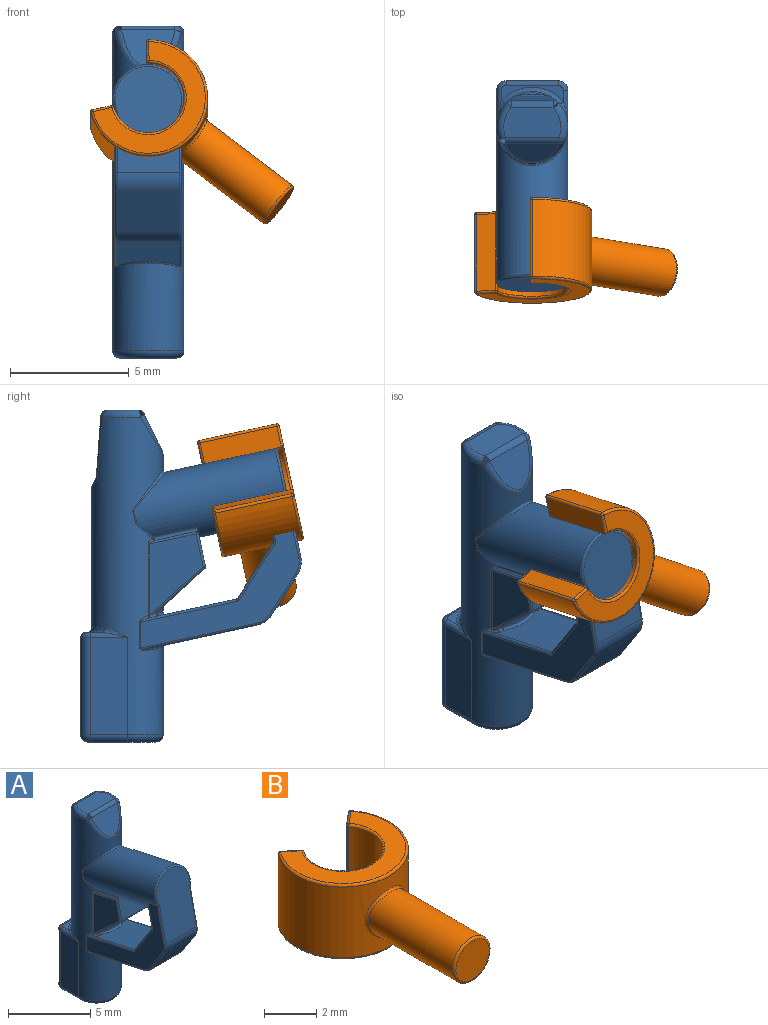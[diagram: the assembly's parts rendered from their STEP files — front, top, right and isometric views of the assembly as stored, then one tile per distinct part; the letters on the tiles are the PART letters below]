
ASSEMBLY  parts=2 mates=1
PART A: 146 faces, bbox 3.3x9.5x14 mm
  f0: bspline ~0.18x0.13mm, area 0mm2, adj f1,f4,f23,f53
  f1: cylinder r=0.1mm len=0.17mm, axis (1,0,0), area 0mm2, adj f0,f11,f53,f72
  f2: cylinder r=0.1mm len=0.18mm, axis (1,0,0), area 0mm2, adj f3,f11,f53,f69
  f3: bspline ~0.18x0.13mm, area 0mm2, adj f2,f18,f53,f71
  f4: bspline ~0.43x0.32mm, area 0.1mm2, adj f0,f23,f53,f77
  f5: plane 2.6x0.67mm, normal (0,0,1), area 0.6mm2, adj f60,f61,f62,f64,f66,f68
  f6: cylinder r=1.5mm len=1.72mm, axis (0,0,-1), area 0mm2, adj f22,f70
  f7: cylinder r=1.5mm len=13.36mm, axis (0,0,-1), area 80.6mm2, adj f15,f17,f20,f25,f27,f29,f32,f35
  f8: plane 3.42x2.25mm, normal (1,0,0), area 4.8mm2, adj f23,f26,f27,f28
  f9: plane 3.42x2.25mm, normal (-1,0,0), area 4.8mm2, adj f14,f16,f17,f18
  f10: plane 2.2x1.64mm, normal (0,-0.98,0.21), area 3mm2, adj f12,f16,f21,f26,f30,f33
  f11: plane 2.2x2.01mm, normal (0,-0.67,-0.74), area 5.5mm2, adj f1,f2,f18,f21,f22,f23
  f12: cylinder r=1.5mm len=6.87mm, axis (0,0.98,-0.21), area 45.5mm2, adj f10,f30,f32,f33,f35,f36,f37,f39
  f13: plane 4.52x2.83mm, normal (0,-0.98,0.21), area 11.5mm2, adj f36,f103,f104,f105,f106,f122,f123,f124
  f14: cylinder r=0.1mm len=2.07mm, axis (0,-0.98,0.21), area 0.3mm2, adj f9,f15,f16,f30
  f15: bspline ~0.29x0.26mm, area 0mm2, adj f7,f14,f17,f31
  f16: cylinder r=0.1mm len=1.5mm, axis (0,-0.21,-0.98), area 0.2mm2, adj f9,f10,f14,f19,f30
  f17: cylinder r=0.1mm len=3mm, axis (0,0,-1), area 0.2mm2, adj f7,f9,f15,f20
  f18: cylinder r=0.1mm len=2.33mm, axis (0,0.74,-0.67), area 0.4mm2, adj f3,f9,f11,f19,f20,f71
  f19: sphere r=0.1mm, area 0mm2, adj f16,f18,f21
  f20: bspline ~0.07x0.06mm, area 0mm2, adj f7,f17,f18,f73
  f21: cylinder r=0.1mm len=2.2mm, axis (-1,0,0), area 0.2mm2, adj f10,f11,f19,f24
  f22: bspline ~1.83x0.34mm, area 0.2mm2, adj f6,f11,f69,f72
  f23: cylinder r=0.1mm len=2.33mm, axis (0,-0.74,0.67), area 0.4mm2, adj f0,f4,f8,f11,f24,f25
  f24: sphere r=0.1mm, area 0mm2, adj f21,f23,f26
  f25: bspline ~0.1x0.08mm, area 0mm2, adj f7,f23,f27,f77
  f26: cylinder r=0.1mm len=1.5mm, axis (0,0.21,0.98), area 0.2mm2, adj f8,f10,f24,f28,f33
  f27: cylinder r=0.1mm len=3mm, axis (0,0,-1), area 0.2mm2, adj f7,f8,f25,f29
  f28: cylinder r=0.1mm len=2.07mm, axis (0,0.98,-0.21), area 0.3mm2, adj f8,f26,f29,f33
  f29: bspline ~0.32x0.28mm, area 0mm2, adj f7,f27,f28,f34
  f30: cylinder r=0.1mm len=1.86mm, axis (0,-0.98,0.21), area 0.4mm2, adj f10,f12,f14,f16,f31
  f31: sphere r=0.1mm, area 0mm2, adj f15,f30,f32
  f32: bspline ~0.91x0.75mm, area 0.1mm2, adj f7,f12,f31,f43
  f33: cylinder r=0.1mm len=1.86mm, axis (0,0.98,-0.21), area 0.4mm2, adj f10,f12,f26,f28,f34
  f34: sphere r=0.1mm, area 0mm2, adj f29,f33,f35
  f35: bspline ~0.91x0.75mm, area 0.1mm2, adj f7,f12,f34,f38
  f36: torus R=1.4mm, axis (0,0.98,-0.21), area 0.8mm2, adj f12,f13,f83,f87,f100,f101
  f37: bspline ~3x1.86mm, area 0.6mm2, adj f7,f12,f40,f41
  f38: bspline ~0.05x0.03mm, area 0mm2, adj f7,f35,f39
  f39: bspline ~0.56x0.15mm, area 0mm2, adj f7,f12,f38,f40
  f40: bspline ~0.05x0.03mm, area 0mm2, adj f7,f37,f39
  f41: bspline ~0.05x0.03mm, area 0mm2, adj f7,f37,f42
  f42: bspline ~0.56x0.15mm, area 0mm2, adj f7,f12,f41,f43
  f43: bspline ~0.05x0.03mm, area 0mm2, adj f7,f32,f42
  f44: plane 2.24x1.56mm, normal (0,-0.9,0.44), area 2.8mm2, adj f136,f139
  f45: plane 2.4x1.26mm, normal (0,0,1), area 2.8mm2, adj f131,f134,f135,f136
  f46: plane 2.6x1.82mm, normal (0,1,0.07), area 3.9mm2, adj f126,f129,f130,f131
  f47: plane 0.87x0.11mm, normal (0,0.81,0.58), area 0.1mm2, adj f125,f126
  f48: plane 2.86x2.4mm, normal (0,0,-1), area 6.2mm2, adj f140,f141,f142,f143,f144,f145
  f49: plane 6.67x6.39mm, normal (-1,0,0), area 11mm2, adj f74,f78,f81,f84,f87,f88,f90,f91
  f50: plane 4.56x2.62mm, normal (0,-0.21,-0.98), area 10.9mm2, adj f102,f112,f115,f118
  f51: plane 6.67x6.39mm, normal (1,0,0), area 11mm2, adj f80,f86,f89,f93,f95,f97,f99,f101
  f52: plane 2.6x1.34mm, normal (0,0.98,-0.21), area 2.4mm2, adj f91,f92,f96,f97
  f53: plane 3.65x2.64mm, normal (0,0.21,0.98), area 8.3mm2, adj f0,f1,f2,f3,f4,f70,f71,f75
  f54: plane 2.6x2.31mm, normal (0,0.84,0.54), area 7.1mm2, adj f84,f85,f92,f93
  f55: plane 2.62x1.68mm, normal (0,-0.84,-0.54), area 5.2mm2, adj f102,f103,f108,f120
  f56: plane 4.1x1.56mm, normal (1,0,0), area 6.4mm2, adj f7,f60,f65,f140
  f57: plane 4.1x1.56mm, normal (-1,0,0), area 6.4mm2, adj f7,f64,f67,f143
  f58: plane 4.1x2.2mm, normal (0,1,0), area 9mm2, adj f62,f65,f67,f144
  f59: bspline ~1.2x0.43mm, area 0.1mm2, adj f7,f60,f61
  f60: cylinder r=0.2mm len=1.56mm, axis (0,-1,0), area 0.3mm2, adj f5,f56,f59,f66
  f61: torus R=1.7mm, axis (0,0,-1), area 0.9mm2, adj f5,f7,f59,f63
  f62: cylinder r=0.2mm len=2.2mm, axis (1,0,0), area 0.7mm2, adj f5,f58,f66,f68
  f63: bspline ~1.2x0.43mm, area 0.1mm2, adj f7,f61,f64
  f64: cylinder r=0.2mm len=1.56mm, axis (0,1,0), area 0.3mm2, adj f5,f57,f63,f68
  f65: cylinder r=0.4mm len=4.1mm, axis (0,0,1), area 2.6mm2, adj f56,f58,f66,f142
  f66: torus R=0.2mm, axis (0,0,-1), area 0.2mm2, adj f5,f60,f62,f65
  f67: cylinder r=0.4mm len=4.1mm, axis (0,0,1), area 2.6mm2, adj f57,f58,f68,f145
  f68: torus R=0.2mm, axis (0,0,-1), area 0.2mm2, adj f5,f62,f64,f67
  f69: sphere r=0.1mm, area 0mm2, adj f2,f22,f70
  f70: bspline ~1.83x0.39mm, area 0.3mm2, adj f6,f53,f69,f72
  f71: bspline ~0.43x0.32mm, area 0.1mm2, adj f3,f18,f53,f73
  f72: sphere r=0.1mm, area 0mm2, adj f1,f22,f70
  f73: sphere r=0.1mm, area 0mm2, adj f20,f71,f75
  f74: cylinder r=0.1mm len=1.1mm, axis (0,0,-1), area 0mm2, adj f7,f49,f76,f109
  f75: bspline ~0.1x0.08mm, area 0mm2, adj f7,f53,f73,f76
  f76: bspline ~0.46x0.29mm, area 0mm2, adj f7,f74,f75,f78
  f77: sphere r=0.1mm, area 0mm2, adj f4,f25,f79
  f78: cylinder r=0.1mm len=4.05mm, axis (0,-0.98,0.21), area 0.6mm2, adj f49,f53,f76,f81
  f79: bspline ~0.1x0.08mm, area 0mm2, adj f7,f53,f77,f82
  f80: cylinder r=0.1mm len=1.1mm, axis (0,0,-1), area 0mm2, adj f7,f51,f82,f116
  f81: torus R=0.2mm, axis (-1,0,0), area 0mm2, adj f49,f78,f84,f85
  f82: bspline ~0.46x0.3mm, area 0mm2, adj f7,f79,f80,f86
  f83: bspline ~0.46x0.08mm, area 0mm2, adj f36,f87,f104
  f84: cylinder r=0.1mm len=2.36mm, axis (0,-0.54,0.84), area 0.4mm2, adj f49,f54,f81,f88
  f85: cylinder r=0.1mm len=2.6mm, axis (1,0,0), area 0.2mm2, adj f53,f54,f81,f89
  f86: cylinder r=0.1mm len=4.05mm, axis (0,-0.98,0.21), area 0.6mm2, adj f51,f53,f82,f89
  f87: bspline ~0.15x0.1mm, area 0mm2, adj f36,f49,f83,f90,f105
  f88: torus R=0.2mm, axis (-1,0,0), area 0mm2, adj f49,f84,f91,f92
  f89: torus R=0.2mm, axis (1,0,0), area 0mm2, adj f51,f85,f86,f93
  f90: cylinder r=0.1mm len=0.79mm, axis (0,0.98,-0.21), area 0mm2, adj f12,f49,f87,f94
  f91: cylinder r=0.1mm len=1.73mm, axis (0,0.21,0.98), area 0.2mm2, adj f49,f52,f88,f94
  f92: cylinder r=0.1mm len=2.6mm, axis (1,0,0), area 0.2mm2, adj f52,f54,f88,f95
  f93: cylinder r=0.1mm len=2.36mm, axis (0,0.54,-0.84), area 0.4mm2, adj f51,f54,f89,f95
  f94: bspline ~0.44x0.2mm, area 0mm2, adj f12,f90,f91,f96
  f95: torus R=0.2mm, axis (1,0,0), area 0mm2, adj f51,f92,f93,f97
  f96: torus R=1.6mm, axis (0,-0.98,0.21), area 0.5mm2, adj f12,f52,f94,f98
  f97: cylinder r=0.1mm len=1.73mm, axis (0,-0.21,-0.98), area 0.2mm2, adj f51,f52,f95,f98
  f98: bspline ~0.49x0.24mm, area 0mm2, adj f12,f96,f97,f99
  f99: cylinder r=0.1mm len=0.79mm, axis (0,0.98,-0.21), area 0mm2, adj f12,f51,f98,f101
  f100: bspline ~0.55x0.12mm, area 0mm2, adj f36,f101,f123
  f101: bspline ~0.15x0.1mm, area 0mm2, adj f36,f51,f99,f100,f124
  f102: cylinder r=1mm len=2.62mm, axis (-1,0,0), area 2.1mm2, adj f50,f55,f110,f119
  f103: cylinder r=1mm len=2.62mm, axis (-1,0,0), area 2.1mm2, adj f13,f55,f107,f121
  f104: bspline ~0.47x0.1mm, area 0mm2, adj f13,f83,f105
  f105: bspline ~0.18x0.11mm, area 0mm2, adj f13,f87,f104,f106
  f106: cylinder r=0.09mm len=2.59mm, axis (0,0.21,0.98), area 0.4mm2, adj f13,f49,f105,f107
  f107: torus R=0.91mm, axis (-1,0,0), area 0.1mm2, adj f49,f103,f106,f108
  f108: cylinder r=0.09mm len=1.73mm, axis (0,-0.54,0.84), area 0.3mm2, adj f49,f55,f107,f110
  f109: bspline ~0.11x0.1mm, area 0mm2, adj f74,f111,f112
  f110: torus R=0.91mm, axis (-1,0,0), area 0.1mm2, adj f49,f102,f108,f112
  f111: bspline ~0.1x0.06mm, area 0mm2, adj f7,f109,f113
  f112: cylinder r=0.09mm len=4.89mm, axis (0,-0.98,0.21), area 0.7mm2, adj f49,f50,f109,f110,f113
  f113: bspline ~0.37x0.18mm, area 0mm2, adj f7,f111,f112,f115
  f114: bspline ~0.1x0.06mm, area 0mm2, adj f7,f116,f117
  f115: bspline ~2.62x0.72mm, area 0.4mm2, adj f7,f50,f113,f117
  f116: bspline ~0.11x0.11mm, area 0mm2, adj f80,f114,f118
  f117: bspline ~0.38x0.18mm, area 0mm2, adj f7,f114,f115,f118
  f118: cylinder r=0.09mm len=4.89mm, axis (0,-0.98,0.21), area 0.7mm2, adj f50,f51,f116,f117,f119
  f119: torus R=0.91mm, axis (1,0,0), area 0.1mm2, adj f51,f102,f118,f120
  f120: cylinder r=0.09mm len=1.73mm, axis (0,0.54,-0.84), area 0.3mm2, adj f51,f55,f119,f121
  f121: torus R=0.91mm, axis (1,0,0), area 0.1mm2, adj f51,f103,f120,f122
  f122: cylinder r=0.09mm len=2.59mm, axis (0,-0.21,-0.98), area 0.4mm2, adj f13,f51,f121,f124
  f123: bspline ~0.52x0.11mm, area 0mm2, adj f13,f100,f124
  f124: bspline ~0.18x0.11mm, area 0mm2, adj f13,f101,f122,f123
  f125: bspline ~1.09x0.29mm, area 0.2mm2, adj f7,f47,f127,f128
  f126: cylinder r=0.3mm len=1.31mm, axis (-1,0,0), area 0.2mm2, adj f46,f47,f127,f128
  f127: bspline ~0.49x0.4mm, area 0.1mm2, adj f7,f125,f126,f129
  f128: bspline ~0.5x0.44mm, area 0.1mm2, adj f7,f125,f126,f130
  f129: bspline ~2.55x0.44mm, area 0.5mm2, adj f7,f46,f127,f132
  f130: bspline ~2.55x0.44mm, area 0.5mm2, adj f7,f46,f128,f133
  f131: cylinder r=0.3mm len=1.74mm, axis (1,0,0), area 0.8mm2, adj f45,f46,f132,f133
  f132: sphere r=0.3mm, area 0.1mm2, adj f129,f131,f134
  f133: sphere r=0.3mm, area 0.1mm2, adj f130,f131,f135
  f134: torus R=1.2mm, axis (0,0,-1), area 0.7mm2, adj f7,f45,f132,f137
  f135: torus R=1.2mm, axis (0,0,-1), area 0.7mm2, adj f7,f45,f133,f138
  f136: cylinder r=0.3mm len=2.24mm, axis (1,0,0), area 0.7mm2, adj f44,f45,f137,f138
  f137: sphere r=0.3mm, area 0.1mm2, adj f134,f136,f139
  f138: sphere r=0.3mm, area 0.1mm2, adj f135,f136,f139
  f139: bspline ~2.8x1.69mm, area 1.2mm2, adj f7,f44,f137,f138
  f140: cylinder r=0.3mm len=1.56mm, axis (0,1,0), area 0.7mm2, adj f48,f56,f141,f142
  f141: torus R=1.2mm, axis (0,0,1), area 2.1mm2, adj f7,f48,f140,f143
  f142: torus R=0.1mm, axis (0,0,1), area 0.2mm2, adj f48,f65,f140,f144
  f143: cylinder r=0.3mm len=1.56mm, axis (0,-1,0), area 0.7mm2, adj f48,f57,f141,f145
  f144: cylinder r=0.3mm len=2.2mm, axis (-1,0,0), area 1mm2, adj f48,f58,f142,f145
  f145: torus R=0.1mm, axis (0,0,1), area 0.2mm2, adj f48,f67,f143,f144
PART B: 27 faces, bbox 5.4x8.7x3.5 mm
  f0: cylinder r=1.5mm len=3.3mm, axis (0,0,-1), area 22.2mm2, adj f1,f10,f16,f19
  f1: plane 3.3x0.69mm, normal (0.64,0.77,0), area 3mm2, adj f0,f20,f23,f26
  f2: cylinder r=2.5mm len=5mm, axis (0,0,-1), area 33mm2, adj f8,f13,f21,f22,f26
  f3: plane 3.3x0.61mm, normal (-0.64,0.77,0), area 2.6mm2, adj f10,f12,f13,f14
  f4: plane 4.8x3.86mm, normal (0,0,1), area 7.1mm2, adj f12,f16,f20,f21
  f5: plane 4.8x3.86mm, normal (0,0,-1), area 7.1mm2, adj f14,f19,f22,f23
  f6: plane 1.8x1.8mm, normal (0,-1,0), area 2.5mm2, adj f9
  f7: cylinder r=1mm len=4.54mm, axis (0,-1,0), area 27.8mm2, adj f8,f9
  f8: bspline ~2.2x2.12mm, area 0.9mm2, adj f2,f7
  f9: torus R=0.9mm, axis (0,-1,0), area 1mm2, adj f6,f7
  f10: cylinder r=0.1mm len=3.3mm, axis (0,0,-1), area 0.5mm2, adj f0,f3,f11,f15
  f11: sphere r=0.1mm, area 0mm2, adj f10,f12,f16
  f12: cylinder r=0.1mm len=0.68mm, axis (0.77,0.64,0), area 0.1mm2, adj f3,f4,f11,f17
  f13: cylinder r=0.1mm len=3.3mm, axis (0,0,-1), area 0.5mm2, adj f2,f3,f17,f18
  f14: cylinder r=0.1mm len=0.68mm, axis (-0.77,-0.64,0), area 0.1mm2, adj f3,f5,f15,f18
  f15: sphere r=0.1mm, area 0mm2, adj f10,f14,f19
  f16: torus R=1.6mm, axis (0,0,1), area 1.1mm2, adj f0,f4,f11,f20
  f17: sphere r=0.1mm, area 0mm2, adj f12,f13,f21
  f18: sphere r=0.1mm, area 0mm2, adj f13,f14,f22
  f19: torus R=1.6mm, axis (0,0,1), area 1.1mm2, adj f0,f5,f15,f23
  f20: cylinder r=0.1mm len=0.75mm, axis (0.77,-0.64,0), area 0.1mm2, adj f1,f4,f16,f24
  f21: torus R=2.4mm, axis (0,0,1), area 1.7mm2, adj f2,f4,f17,f24
  f22: torus R=2.4mm, axis (0,0,1), area 1.7mm2, adj f2,f5,f18,f25
  f23: cylinder r=0.1mm len=0.75mm, axis (-0.77,0.64,0), area 0.1mm2, adj f1,f5,f19,f25
  f24: sphere r=0.1mm, area 0mm2, adj f20,f21,f26
  f25: sphere r=0.1mm, area 0mm2, adj f22,f23,f26
  f26: cylinder r=0.1mm len=3.3mm, axis (0,0,-1), area 0.5mm2, adj f1,f2,f24,f25
PLACE A t=(-0.01,1.4,-15.87)mm fixed
PLACE B rot(axis=(-0.36,0.73,0.59),147.9deg) t=(-0.01,-5.48,10.84)mm
MATE cylindrical B.f0 <-> A.f12  axis (0,0.98,-0.21) through (-0.01,-2.16,10.12)mm
